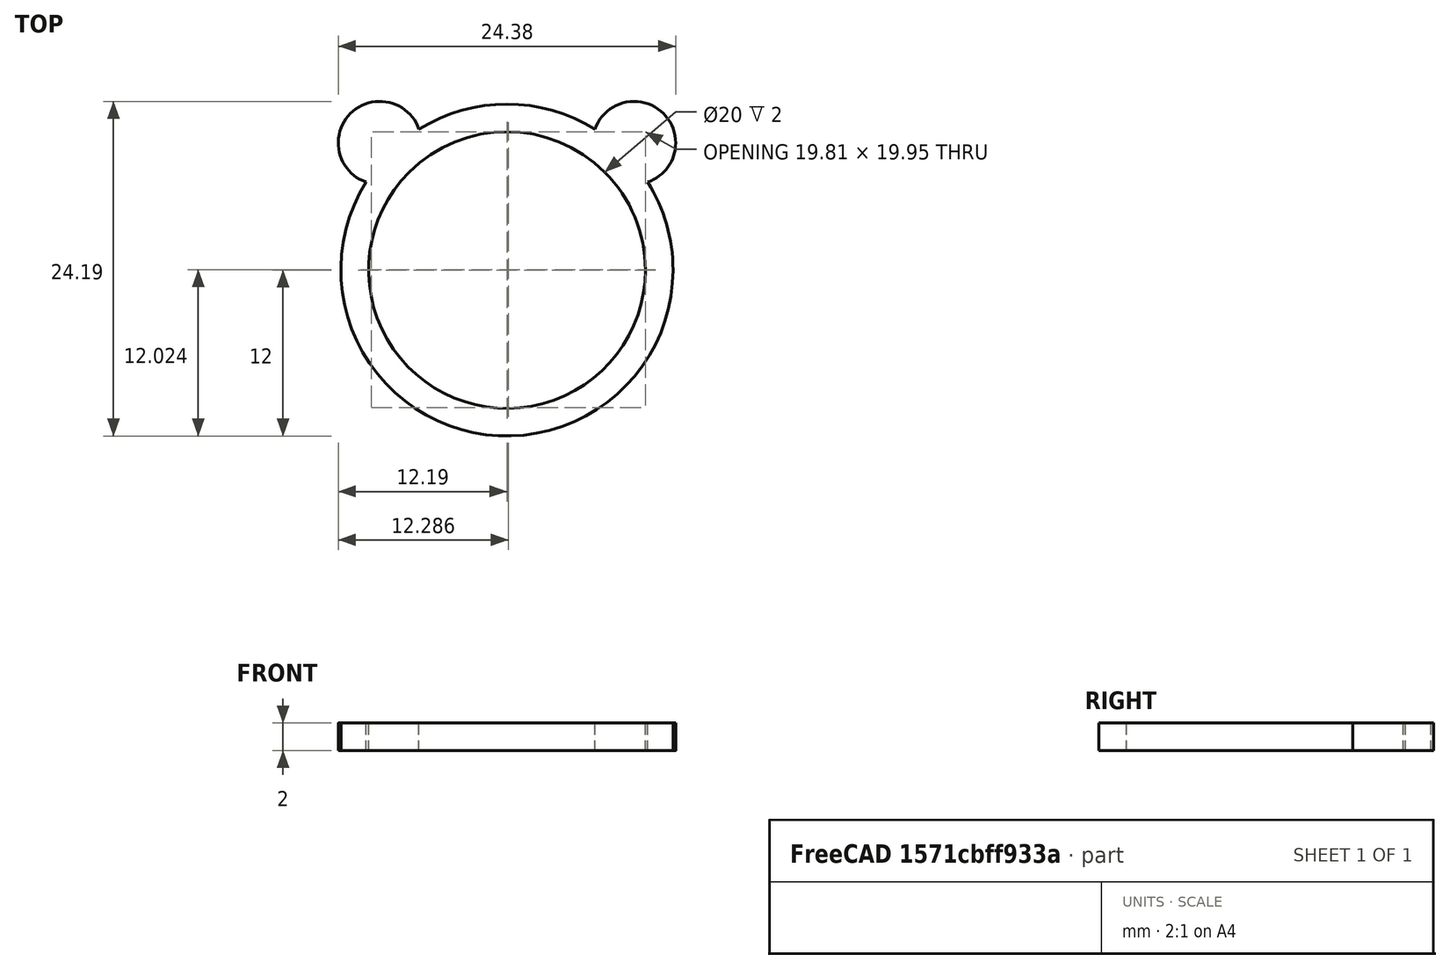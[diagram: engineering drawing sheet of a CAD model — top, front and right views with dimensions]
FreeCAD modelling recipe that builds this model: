
FCSTD DOCUMENT  (FreeCAD 0.17R13217 (Git))
Label: 03-1-anillo-basico
License: All rights reserved
LicenseURL: http://en.wikipedia.org/wiki/All_rights_reserved
objects: TechDraw::DrawViewDimension×4, Sketcher::SketchObject×2, PartDesign::Pad×2, TechDraw::DrawProjGroupItem×2, TechDraw::DrawViewAnnotation×2, PartDesign::Body×1, TechDraw::DrawSVGTemplate×1, TechDraw::DrawProjGroup×1, TechDraw::DrawViewPart×1, TechDraw::DrawPage×1
note: 7 computed .brp shape members not serialized (recipe doc carries the construction recipe); baked Part::Feature solids carry a one-line shape summary decoded from their .brp

FEATURE [Sketcher::SketchObject] Sketch
  MapMode = 5
  Support = -> [XY_Plane]
  sketch-geometry (3):
    g0: Circle CenterX=0 CenterY=0 CenterZ=0 NormalX=0 NormalY=0 NormalZ=1 AngleXU=0 Radius=10
    g1: Circle CenterX=0 CenterY=0 CenterZ=0 NormalX=0 NormalY=0 NormalZ=1 AngleXU=0 Radius=12
    g2: LineSegment [constr] StartX=10 StartY=0 StartZ=0 EndX=12 EndY=0 EndZ=0
  constraints (8):
    c: Coincident(g0,g-1)
    c: Coincident(g1,g-1)
    c: Radius(g0) = 10
    c: PointOnObject(g2,g0)
    c: PointOnObject(g2,g1)
    c: Horizontal(g2)
    c: PointOnObject(g2,g-1)
    c: DistanceX(g2,g2) = 2
FEATURE [PartDesign::Pad] Pad  label="Anillo-base"
  Length = 2
  Length2 = 100
  Profile = -> Sketch
  Refine = true
  Reversed = true
  Type = 0
FEATURE [Sketcher::SketchObject] Sketch001
  MapMode = 5
  Support = -> [XY_Plane]
  sketch-geometry (5):
    g0: Circle CenterX=-9.19239 CenterY=9.19239 CenterZ=0 NormalX=0 NormalY=0 NormalZ=1 AngleXU=0 Radius=3
    g1: LineSegment [constr] StartX=-9.19239 StartY=9.19239 StartZ=0 EndX=0 EndY=0 EndZ=0
    g2: GeomPoint X=-7.07107 Y=7.07107 Z=0
    g3: Circle [constr] CenterX=0 CenterY=0 CenterZ=0 NormalX=0 NormalY=0 NormalZ=1 AngleXU=0 Radius=10
    g4: Circle CenterX=9.19239 CenterY=9.19239 CenterZ=0 NormalX=0 NormalY=0 NormalZ=1 AngleXU=0 Radius=3
  constraints (11):
    c: Coincident(g1,g0)
    c: Coincident(g1,g-1)
    c: PointOnObject(g2,g0)
    c: PointOnObject(g2,g1)
    c: Angle(g-2,g1) = 0.785398
    c: Coincident(g3,g-1)
    c: Radius(g3) = 10
    c: PointOnObject(g2,g3)
    c: Radius(g0) = 3
    c: Symmetric(g0,g4,g-2)
    c: Equal(g0,g4)
FEATURE [PartDesign::Pad] Pad001  label="orejas"
  BaseFeature = -> Pad
  Length = 2
  Length2 = 100
  Profile = -> Sketch001
  Refine = true
  Reversed = true
  Type = 0
FEATURE [PartDesign::Body] Body
  Group = -> [Sketch,Pad,Sketch001,Pad001]
  Origin = -> Origin
  Tip = -> Pad001
FEATURE [TechDraw::DrawSVGTemplate] Template
  EditableTexts = Designed_by_Name=Designed by Name; Drawing_number=Drawing number; FC-Date=Date; FC-SC=Scale; FC-SH=Sheet; FC-Title=Title; Subtitle=Subtitle; Weight=Weight
  Height = 210
  Orientation = 1
  Width = 297
FEATURE [TechDraw::DrawProjGroupItem] ProjItem  label="Front"
  ArcCenterMarks = true
  CenterScale = 2
  CoarseView = false
  Direction = (0,-1,0)
  ExtraWidth = 1.4
  Focus = 100
  HardHidden = false
  HiddenWidth = 0.35
  HorizCenterLine = false
  IsoCount = 0
  IsoHidden = false
  IsoVisible = false
  IsoWidth = 0.5
  KeepLabel = false
  LineWidth = 0.7
  LockPosition = false
  Perspective = false
  Rotation = 0
  RotationVector = (1,0,0)
  ScaleType = 0
  SeamHidden = false
  SeamVisible = false
  ShowSectionLine = true
  SmoothHidden = false
  SmoothVisible = false
  Source = -> [Pad001]
  Type = 0
  VertCenterLine = false
  X = 0
  Y = 0
FEATURE [TechDraw::DrawProjGroupItem] ProjItem001  label="Top"
  ArcCenterMarks = true
  CenterScale = 2
  CoarseView = false
  Direction = (0,0,1)
  ExtraWidth = 1.4
  Focus = 100
  HardHidden = false
  HiddenWidth = 0.35
  HorizCenterLine = false
  IsoCount = 0
  IsoHidden = false
  IsoVisible = false
  IsoWidth = 0.5
  KeepLabel = false
  LineWidth = 0.7
  LockPosition = false
  Perspective = false
  Rotation = 0
  RotationVector = (1,0,0)
  ScaleType = 0
  SeamHidden = false
  SeamVisible = false
  ShowSectionLine = true
  SmoothHidden = false
  SmoothVisible = false
  Source = -> [Pad001]
  Type = 4
  VertCenterLine = false
  X = 0
  Y = -63.3848
FEATURE [TechDraw::DrawProjGroup] ProjGroup
  Anchor = -> ProjItem
  AutoDistribute = true
  CubeDirs = (6) [(0,0,-1),(0,-1,0),(-1,0,0),(0,1,0),(1,0,0),(0,0,1)]
  CubeRotations = (6) [(1,0,0),(1,0,0),(0,1,0),(-1,0,0),(0,-1,0),(1,0,0)]
  KeepLabel = false
  LockPosition = false
  ProjectionType = 0
  Rotation = 0
  Scale = 2
  ScaleType = 2
  Source = -> [Pad001]
  Views = -> [ProjItem,ProjItem001]
  X = 67.9014
  Y = 160.458
  spacingX = 15
  spacingY = 15
FEATURE [TechDraw::DrawViewPart] View
  ArcCenterMarks = true
  CenterScale = 2
  CoarseView = false
  Direction = (1,-1,1)
  ExtraWidth = 1.4
  Focus = 100
  HardHidden = false
  HiddenWidth = 0.35
  HorizCenterLine = false
  IsoCount = 0
  IsoHidden = false
  IsoVisible = false
  IsoWidth = 0.5
  KeepLabel = false
  LineWidth = 0.7
  LockPosition = false
  Perspective = false
  Rotation = 0
  Scale = 3
  ScaleType = 0
  SeamHidden = false
  SeamVisible = false
  ShowSectionLine = true
  SmoothHidden = false
  SmoothVisible = false
  Source = -> [Pad001]
  VertCenterLine = false
  X = 207.655
  Y = 117.57
FEATURE [TechDraw::DrawViewDimension] Dimension
  Font = osifont
  Fontsize = 3.5
  FormatSpec = %.2f
  KeepLabel = false
  LineWidth = 0.5
  LockPosition = false
  MeasureType = 1
  References2D = -> [ProjItem001]
  Rotation = 0
  Scale = 4
  ScaleType = 0
  Type = 5
  X = -43.1696
  Y = 13.4847
FEATURE [TechDraw::DrawViewDimension] Dimension001
  Font = osifont
  Fontsize = 3.5
  FormatSpec = %.2f
  KeepLabel = false
  LineWidth = 0.5
  LockPosition = false
  MeasureType = 1
  References2D = -> [ProjItem001]
  Rotation = 0
  Scale = 4
  ScaleType = 0
  Type = 1
  X = 52.7465
  Y = 22.4296
FEATURE [TechDraw::DrawViewDimension] Dimension002
  Font = osifont
  Fontsize = 3.5
  FormatSpec = %.2f
  KeepLabel = false
  LineWidth = 0.5
  LockPosition = false
  MeasureType = 1
  References2D = -> [ProjItem001]
  Rotation = 0
  Scale = 4
  ScaleType = 0
  Type = 5
  X = 12.0775
  Y = -38.2042
FEATURE [TechDraw::DrawViewDimension] Dimension003
  Font = osifont
  Fontsize = 3.5
  FormatSpec = %.2f
  KeepLabel = false
  LineWidth = 0.5
  LockPosition = false
  MeasureType = 1
  References2D = -> [ProjItem]
  Rotation = 0
  Scale = 4
  ScaleType = 0
  Type = 2
  X = 30.3991
  Y = -16.4319
FEATURE [TechDraw::DrawViewAnnotation] Annotation
  Font = osifont
  KeepLabel = false
  LineSpace = 80
  LockPosition = false
  MaxWidth = -1
  Rotation = 0
  Scale = 4
  ScaleType = 0
  Text = Anillo "osito"
  TextSize = 8
  TextStyle = 0
  X = 201.376
  Y = 177.901
FEATURE [TechDraw::DrawViewAnnotation] Annotation001
  Font = osifont
  KeepLabel = false
  LineSpace = 80
  LockPosition = false
  MaxWidth = -1
  Rotation = 0
  Scale = 4
  ScaleType = 0
  Text = Orejas a 45 grados
  TextSize = 5
  TextStyle = 0
  X = 71.0988
  Y = 47.6241
FEATURE [TechDraw::DrawPage] Page  label="Planos"
  KeepUpdated = true
  ProjectionType = 0
  Scale = 4
  Template = -> Template
  Views = -> [ProjGroup,View,Dimension,Dimension001,Dimension002,Dimension003,Annotation,Annotation001]
